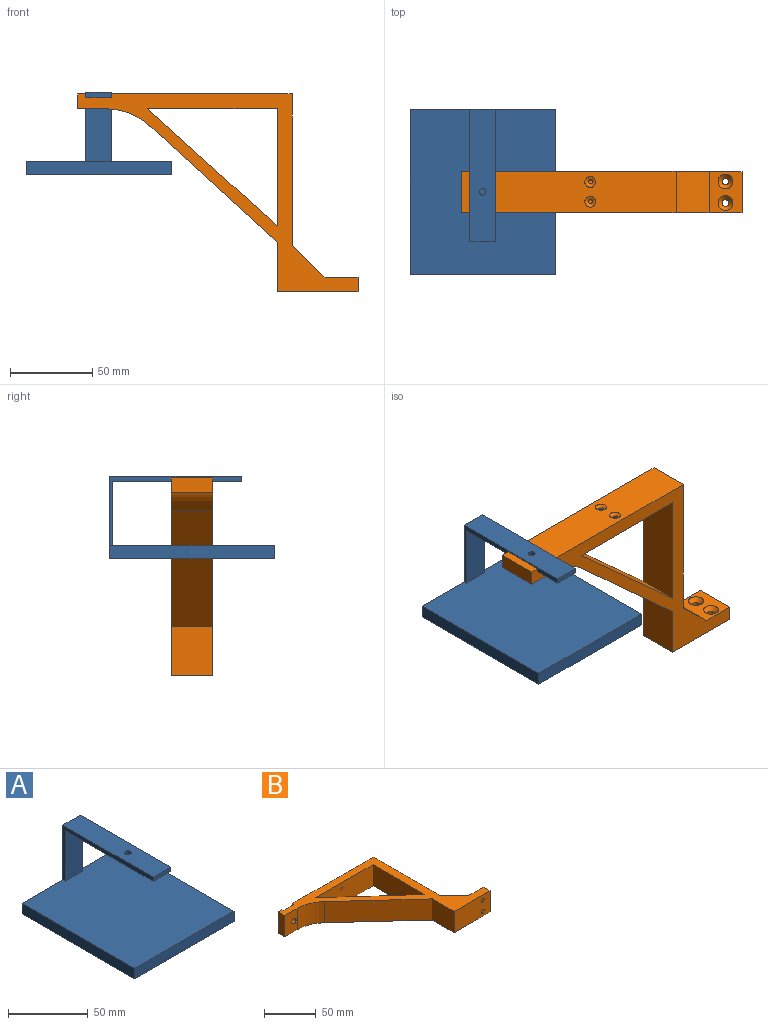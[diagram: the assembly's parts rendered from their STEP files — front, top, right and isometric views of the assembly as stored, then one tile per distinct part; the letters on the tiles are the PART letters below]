
ASSEMBLY  parts=2 mates=1
PART A: 13 faces, bbox 88x100x50 mm
  f0: plane 38.87x15.5mm, normal (0,-1,0), area 602.5mm2, adj f1,f7,f8,f10
  f1: plane 100x88mm, normal (0,0,1), area 8769mm2, adj f0,f2,f3,f4,f5,f7,f8
  f2: plane 88x8mm, normal (0,-1,0), area 704mm2, adj f1,f3,f5,f6
  f3: plane 100x8mm, normal (1,0,0), area 800mm2, adj f1,f2,f4,f6
  f4: plane 88x50mm, normal (0,1,0), area 1355mm2, adj f1,f3,f5,f6,f7,f8,f9
  f5: plane 100x8mm, normal (-1,0,0), area 800mm2, adj f1,f2,f4,f6
  f6: plane 100x88mm, normal (0,0,-1), area 8800mm2, adj f2,f3,f4,f5
  f7: plane 80x42mm, normal (-1,0,0), area 327.9mm2, adj f0,f1,f4,f9,f10,f11
  f8: plane 80x42mm, normal (1,0,0), area 327.9mm2, adj f0,f1,f4,f9,f10,f11
  f9: plane 80x15.5mm, normal (0,0,1), area 1227.4mm2, adj f4,f7,f8,f11,f12
  f10: plane 78x15.5mm, normal (0,0,-1), area 1196.4mm2, adj f0,f7,f8,f11,f12
  f11: plane 15.5x3.13mm, normal (0,-1,0), area 48.5mm2, adj f7,f8,f9,f10
  f12: cylinder r=2mm len=4mm, axis (0,0,1), area 39.3mm2, adj f9,f10
PART B: 29 faces, bbox 170x120x25 mm
  f0: plane 109.5x25mm, normal (0,1,0), area 2671.1mm2, adj f5,f12,f15,f17,f26,f27
  f1: plane 78.5x25mm, normal (0,-1,0), area 1952.7mm2, adj f5,f6,f7,f15,f24,f25
  f2: plane 49x25mm, normal (0,-1,0), area 1199.9mm2, adj f5,f9,f10,f15,f20,f21
  f3: plane 25x20mm, normal (0,1,0), area 372.8mm2, adj f5,f10,f11,f15,f22,f23
  f4: plane 25x5mm, normal (0,1,0), area 125mm2, adj f5,f13,f15,f16
  f5: plane 170x120mm, normal (0,0,1), area 3516.4mm2, adj f0,f1,f2,f3,f4,f6,f7,f8
  f6: plane 71x25mm, normal (-1,0,0), area 1775mm2, adj f1,f5,f7,f15
  f7: plane 78.5x71mm, normal (0.67,0.74,0), area 2646.1mm2, adj f1,f5,f6,f15
  f8: plane 77.09x70.55mm, normal (-0.68,-0.74,0), area 2612.5mm2, adj f5,f9,f15,f28
  f9: plane 30x25mm, normal (-1,0,0), area 750mm2, adj f2,f5,f8,f15
  f10: plane 25x9mm, normal (1,0,0), area 225mm2, adj f2,f3,f5,f15
  f11: plane 25x20mm, normal (0.69,0.72,0), area 693.9mm2, adj f3,f5,f12,f15
  f12: plane 91.76x25mm, normal (1,0,0), area 2293.9mm2, adj f0,f5,f11,f15
  f13: plane 25x9mm, normal (-1,0,0), area 225mm2, adj f4,f5,f14,f15
  f14: plane 25x17.03mm, normal (0,-1,0), area 397.4mm2, adj f5,f13,f15,f19,f28
  f15: plane 170x120mm, normal (0,0,-1), area 3516.4mm2, adj f0,f1,f2,f3,f4,f6,f7,f8
  f16: plane 25x2mm, normal (1,0,0), area 50mm2, adj f4,f5,f15,f18
  f17: plane 25x2mm, normal (-1,0,0), area 50mm2, adj f0,f5,f15,f18
  f18: plane 25x15.5mm, normal (0,1,0), area 359.2mm2, adj f5,f15,f16,f17,f19
  f19: cylinder r=3mm len=7mm, axis (0,1,0), area 131.9mm2, adj f14,f18
  f20: cylinder r=2mm len=6.5mm, axis (0,1,0), area 81.7mm2, adj f2,f22
  f21: cylinder r=2mm len=6.5mm, axis (0,1,0), area 81.7mm2, adj f2,f23
  f22: cone r=4.5mm half-angle=45deg, axis (0,1,0), area 72.2mm2, adj f3,f20
  f23: cone r=2mm half-angle=45deg, axis (0,1,0), area 72.2mm2, adj f3,f21
  f24: cylinder r=1.25mm len=7mm, axis (0,1,0), area 55mm2, adj f1,f26
  f25: cylinder r=1.25mm len=7mm, axis (0,1,0), area 55mm2, adj f1,f27
  f26: torus R=3.25mm, axis (0,-1,0), area 39mm2, adj f0,f24
  f27: torus R=3.25mm, axis (0,-1,0), area 39mm2, adj f0,f25
  f28: cylinder r=39.82mm len=26.88mm, axis (0,0,1), area 737.8mm2, adj f5,f8,f14,f15
PLACE A t=(-50.42,70.2,-20.8)mm
PLACE B rot(axis=(1,0,0),90deg) t=(1.83,82.7,-31.92)mm fixed
MATE fastened B.f19 <-> A.f12  axis (0,0,1) through (-50.42,70.2,26.08)mm
